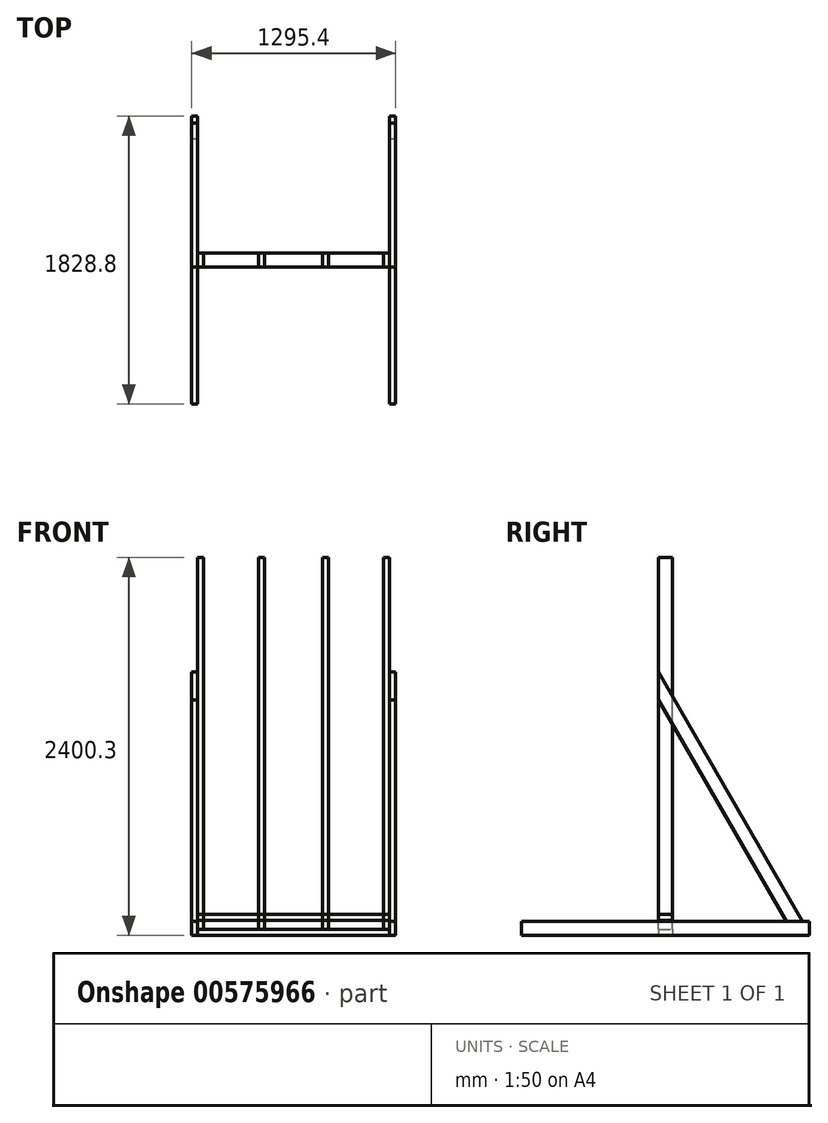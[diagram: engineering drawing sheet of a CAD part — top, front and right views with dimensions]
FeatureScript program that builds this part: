
annotation { "Feature Type Name" : "Feature", "Feature Type Description" : "" }
export const myFeature = defineFeature(function(context is Context, id is Id, definition is map)
    precondition{}
    {
        {
            var Q0;
            Q0=qCreatedBy(makeId("Front.planeOp"),FACE);
            var sketch = newSketch(context, id + "F0", { "sketchPlane" : qUnion([Q0])});
            skLineSegment(sketch, "E0.bottom", {"start": v(0, 0) * mm, "end": v(38.1, 0) * mm});
            skLineSegment(sketch, "E0.top", {"start": v(0, 2362.2) * mm, "end": v(38.1, 2362.2) * mm});
            skLineSegment(sketch, "E0.left", {"start": v(0, 0) * mm, "end": v(0, 2362.2) * mm});
            skLineSegment(sketch, "E0.right", {"start": v(38.1, 0) * mm, "end": v(38.1, 2362.2) * mm});
            skSolve(sketch);
        }
        {
            var Q0;
            Q0 = qSketchRegion(id + "F0", true);
            extrude(context, id + "F1", {"entities" : qUnion([Q0]), "depth" : 88.9 * mm, "offsetDistance" : 25.4 * mm});
        }
        {
            var Q0;
            Q0=makeQuery(id+"F1.opExtrude","SWEPT_BODY",BODY,{"disambiguationData":[OSD([sQuery(id+"F0.wireOp",EDGE,"E0.bottom"),sQuery(id+"F0.wireOp",EDGE,"E0.top"),sQuery(id+"F0.wireOp",EDGE,"E0.left"),sQuery(id+"F0.wireOp",EDGE,"E0.right")])]});
            transform(context, id + "F2", {"entities" : qUnion([Q0]), "transformType" : TransformType.TRANSLATION_3D, "dx" : 387.35 * mm, "dy" : 0 * mm, "dz" : 0 * mm, "makeCopy" : true});
        }
        {
            var Q0;
            Q0=makeQuery(id+"F2.opPattern","COPY",BODY,{"derivedFrom":makeQuery(id+"F1.opExtrude","SWEPT_BODY",BODY,{"disambiguationData":[OSD([sQuery(id+"F0.wireOp",EDGE,"E0.bottom"),sQuery(id+"F0.wireOp",EDGE,"E0.top"),sQuery(id+"F0.wireOp",EDGE,"E0.left"),sQuery(id+"F0.wireOp",EDGE,"E0.right")])]}),"instanceName":"1"});
            transform(context, id + "F3", {"entities" : qUnion([Q0]), "transformType" : TransformType.TRANSLATION_3D, "dx" : 406.4 * mm, "dy" : 0 * mm, "dz" : 0 * mm, "makeCopy" : true});
        }
        {
            var Q0;
            Q0=makeQuery(id+"F3.opPattern","COPY",BODY,{"derivedFrom":makeQuery(id+"F2.opPattern","COPY",BODY,{"derivedFrom":makeQuery(id+"F1.opExtrude","SWEPT_BODY",BODY,{"disambiguationData":[OSD([sQuery(id+"F0.wireOp",EDGE,"E0.bottom"),sQuery(id+"F0.wireOp",EDGE,"E0.top"),sQuery(id+"F0.wireOp",EDGE,"E0.left"),sQuery(id+"F0.wireOp",EDGE,"E0.right")])]}),"instanceName":"1"}),"instanceName":"1"});
            transform(context, id + "F4", {"entities" : qUnion([Q0]), "transformType" : TransformType.TRANSLATION_3D, "dx" : 387.35 * mm, "dy" : 0 * mm, "dz" : 0 * mm, "makeCopy" : true});
        }
        {
            var Q0;
            Q0=qCreatedBy(makeId("Front.planeOp"),FACE);
            var sketch = newSketch(context, id + "F5", { "sketchPlane" : qUnion([Q0])});
            skLineSegment(sketch, "E1.bottom", {"start": v(0, 0) * mm, "end": v(1219.2, 0) * mm});
            skLineSegment(sketch, "E1.top", {"start": v(0, -38.1) * mm, "end": v(1219.2, -38.1) * mm});
            skLineSegment(sketch, "E1.left", {"start": v(0, 0) * mm, "end": v(0, -38.1) * mm});
            skLineSegment(sketch, "E1.right", {"start": v(1219.2, 0) * mm, "end": v(1219.2, -38.1) * mm});
            skSolve(sketch);
        }
        {
            var Q0;
            Q0 = qSketchRegion(id + "F5", true);
            extrude(context, id + "F6", {"entities" : qUnion([Q0]), "depth" : 88.9 * mm, "offsetDistance" : 25.4 * mm});
        }
        {
            var Q0;
            Q0=makeQuery(id+"F6.opExtrude","SWEPT_BODY",BODY,{"disambiguationData":[OSD([sQuery(id+"F5.wireOp",EDGE,"E1.bottom"),sQuery(id+"F5.wireOp",EDGE,"E1.top"),sQuery(id+"F5.wireOp",EDGE,"E1.left"),sQuery(id+"F5.wireOp",EDGE,"E1.right")])]});
            transform(context, id + "F7", {"entities" : qUnion([Q0]), "transformType" : TransformType.TRANSLATION_3D, "dx" : 0 * mm, "dy" : 0 * mm, "dz" : ((8 * 12) - 1.5) * mm, "makeCopy" : true});
        }
        {
            var Q0;
            Q0=makeQuery(id+"F6.opExtrude","SWEPT_FACE",FACE,{"disambiguationData":[OSD([sQuery(id+"F5.wireOp",EDGE,"E1.left")])]});
            var sketch = newSketch(context, id + "F8", { "sketchPlane" : qUnion([Q0])});
            skLineSegment(sketch, "E2.bottom", {"start": v(958.85, 50.8) * mm, "end": v(-869.95, 50.8) * mm});
            skLineSegment(sketch, "E2.top", {"start": v(958.85, -38.1) * mm, "end": v(-869.95, -38.1) * mm});
            skLineSegment(sketch, "E2.left", {"start": v(958.85, 50.8) * mm, "end": v(958.85, -38.1) * mm});
            skLineSegment(sketch, "E2.right", {"start": v(-869.95, 50.8) * mm, "end": v(-869.95, -38.1) * mm});
            skSolve(sketch);
        }
        {
            var Q0;
            Q0 = qSketchRegion(id + "F8", true);
            extrude(context, id + "F9", {"entities" : qUnion([Q0]), "depth" : 38.1 * mm, "offsetDistance" : 25.4 * mm});
        }
        {
            var Q0;
            Q0=makeQuery(id+"F9.opExtrude","SWEPT_BODY",BODY,{"disambiguationData":[OSD([sQuery(id+"F8.wireOp",EDGE,"E2.bottom"),sQuery(id+"F8.wireOp",EDGE,"E2.top"),sQuery(id+"F8.wireOp",EDGE,"E2.left"),sQuery(id+"F8.wireOp",EDGE,"E2.right")])]});
            transform(context, id + "F10", {"entities" : qUnion([Q0]), "transformType" : TransformType.TRANSLATION_3D, "dx" : 1257.3 * mm, "dy" : 0 * mm, "dz" : 0 * mm, "makeCopy" : true});
        }
        {
            var Q0;
            Q0=makeQuery(id+"F10.opPattern","COPY",FACE,{"derivedFrom":makeQuery(id+"F9.opExtrude","CAP_FACE",FACE,{"disambiguationData":[OSD([sQuery(id+"F8.wireOp",EDGE,"E2.bottom"),sQuery(id+"F8.wireOp",EDGE,"E2.top"),sQuery(id+"F8.wireOp",EDGE,"E2.left"),sQuery(id+"F8.wireOp",EDGE,"E2.right")])],"isStart":false}),"instanceName":"1"});
            var sketch = newSketch(context, id + "F11", { "sketchPlane" : qUnion([Q0])});
            skLineSegment(sketch, "E3", {"start": v(-825.5, 50.8) * mm, "end": v(0, 1480.6) * mm});
            skLineSegment(sketch, "E4", {"start": v(0, 1480.6) * mm, "end": v(0, 1302.8) * mm});
            skLineSegment(sketch, "E5", {"start": v(0, 1302.8) * mm, "end": v(-722.85, 50.8) * mm});
            skLineSegment(sketch, "E6", {"start": v(-825.5, 50.8) * mm, "end": v(-722.85, 50.8) * mm});
            skLineSegment(sketch, "E7", {"start": v(0, 1480.6) * mm, "end": v(88.9, 1634.59) * mm});
            skLineSegment(sketch, "E8", {"start": v(0, 1302.8) * mm, "end": v(88.9, 1456.79) * mm});
            skLineSegment(sketch, "E9", {"start": v(88.9, 1634.59) * mm, "end": v(88.9, 1456.79) * mm});
            skSolve(sketch);
        }
        {
            var Q0;
            Q0 = qSketchRegion(id + "F11", true);
            extrude(context, id + "F12", {"entities" : qUnion([Q0]), "oppositeDirection" : true, "depth" : 38.1 * mm, "offsetDistance" : 25.4 * mm});
        }
        {
            var Q0;
            Q0=makeQuery(id+"F12.opExtrude","SWEPT_BODY",BODY,{"disambiguationData":[OSD([sQuery(id+"F11.wireOp",EDGE,"E3"),sQuery(id+"F11.wireOp",EDGE,"E4"),sQuery(id+"F11.wireOp",EDGE,"E5"),sQuery(id+"F11.wireOp",EDGE,"1W0fkmu6-52x2-68E4-ANrA-ky8dyzSj9vcL")])]});
            transform(context, id + "F13", {"entities" : qUnion([Q0]), "transformType" : TransformType.TRANSLATION_3D, "dx" : -1257.3 * mm, "dy" : 0 * mm, "dz" : 0 * mm, "makeCopy" : true});
        }
        {
            var Q0;
            Q0=qCreatedBy(makeId("Right.planeOp"),FACE);
            var sketch = newSketch(context, id + "F14", { "sketchPlane" : qUnion([Q0])});
            skLineSegment(sketch, "E10.bottom", {"start": v(0, 1803.4) * mm, "end": v(-1981.2, 1803.4) * mm});
            skLineSegment(sketch, "E10.top", {"start": v(0, 1892.3) * mm, "end": v(-1981.2, 1892.3) * mm});
            skLineSegment(sketch, "E10.left", {"start": v(0, 1803.4) * mm, "end": v(0, 1892.3) * mm});
            skLineSegment(sketch, "E10.right", {"start": v(-1981.2, 1803.4) * mm, "end": v(-1981.2, 1892.3) * mm});
            skSolve(sketch);
        }
        {
            var Q0;
            Q0 = qSketchRegion(id + "F14", true);
            extrude(context, id + "F15", {"entities" : qUnion([Q0]), "oppositeDirection" : true, "depth" : 38.1 * mm, "offsetDistance" : 25.4 * mm});
        }
        {
            var Q0;
            Q0=makeQuery(id+"F15.opExtrude","SWEPT_BODY",BODY,{"disambiguationData":[OSD([sQuery(id+"F14.wireOp",EDGE,"E10.bottom"),sQuery(id+"F14.wireOp",EDGE,"E10.top"),sQuery(id+"F14.wireOp",EDGE,"E10.left"),sQuery(id+"F14.wireOp",EDGE,"E10.right")])]});
            transform(context, id + "F16", {"entities" : qUnion([Q0]), "transformType" : TransformType.TRANSLATION_3D, "dx" : 1257.3 * mm, "dy" : 0 * mm, "dz" : 0 * mm, "makeCopy" : true});
        }
        {
            var Q0;
            Q0=makeQuery(id+"F15.opExtrude","SWEPT_BODY",BODY,{"disambiguationData":[OSD([sQuery(id+"F14.wireOp",EDGE,"E10.bottom"),sQuery(id+"F14.wireOp",EDGE,"E10.top"),sQuery(id+"F14.wireOp",EDGE,"E10.left"),sQuery(id+"F14.wireOp",EDGE,"E10.right")])]});
            transform(context, id + "F17", {"entities" : qUnion([Q0]), "transformType" : TransformType.TRANSLATION_3D, "dx" : 0 * mm, "dy" : 0 * mm, "dz" : -1524 * mm, "makeCopy" : true});
        }
        {
            var Q0;
            Q0=makeQuery(id+"F17.opPattern","COPY",BODY,{"derivedFrom":makeQuery(id+"F15.opExtrude","SWEPT_BODY",BODY,{"disambiguationData":[OSD([sQuery(id+"F14.wireOp",EDGE,"E10.bottom"),sQuery(id+"F14.wireOp",EDGE,"E10.top"),sQuery(id+"F14.wireOp",EDGE,"E10.left"),sQuery(id+"F14.wireOp",EDGE,"E10.right")])]}),"instanceName":"1"});
            transform(context, id + "F18", {"entities" : qUnion([Q0]), "transformType" : TransformType.TRANSLATION_3D, "dx" : 1257.3 * mm, "dy" : 0 * mm, "dz" : 0 * mm, "makeCopy" : true});
        }
        {
            var Q0;
            Q0=makeQuery(id+"F18.opPattern","COPY",FACE,{"derivedFrom":makeQuery(id+"F17.opPattern","COPY",FACE,{"derivedFrom":makeQuery(id+"F15.opExtrude","CAP_FACE",FACE,{"disambiguationData":[OSD([sQuery(id+"F14.wireOp",EDGE,"E10.bottom"),sQuery(id+"F14.wireOp",EDGE,"E10.top"),sQuery(id+"F14.wireOp",EDGE,"E10.left"),sQuery(id+"F14.wireOp",EDGE,"E10.right")])],"isStart":true}),"instanceName":"1"}),"instanceName":"1"});
            var sketch = newSketch(context, id + "F19", { "sketchPlane" : qUnion([Q0])});
            skLineSegment(sketch, "E11", {"start": v(-1900.94, 1930.52) * mm, "end": v(-1114.62, 279.4) * mm});
            skLineSegment(sketch, "E12", {"start": v(-1114.62, 279.4) * mm, "end": v(-1194.88, 241.18) * mm});
            skLineSegment(sketch, "E13", {"start": v(-1981.2, 1892.3) * mm, "end": v(-1194.88, 241.18) * mm});
            skLineSegment(sketch, "E14", {"start": v(-1900.94, 1930.52) * mm, "end": v(-1981.2, 1892.3) * mm});
            skSolve(sketch);
        }
        {
            var Q0;
            Q0 = qSketchRegion(id + "F19", true);
            extrude(context, id + "F20", {"entities" : qUnion([Q0]), "depth" : 38.1 * mm, "offsetDistance" : 25.4 * mm});
        }
        {
            var Q0;
            Q0=makeQuery(id+"F20.opExtrude","SWEPT_BODY",BODY,{"disambiguationData":[OSD([sQuery(id+"F19.wireOp",EDGE,"E11"),sQuery(id+"F19.wireOp",EDGE,"E12"),sQuery(id+"F19.wireOp",EDGE,"E13"),sQuery(id+"F19.wireOp",EDGE,"E14")])]});
            transform(context, id + "F21", {"entities" : qUnion([Q0]), "transformType" : TransformType.TRANSLATION_3D, "dx" : -1333.5 * mm, "dy" : 0 * mm, "dz" : 0 * mm, "makeCopy" : true});
        }
        {
            var Q0;
            Q0=makeQuery(id+"F21.opPattern","COPY",BODY,{"derivedFrom":makeQuery(id+"F20.opExtrude","SWEPT_BODY",BODY,{"disambiguationData":[OSD([sQuery(id+"F19.wireOp",EDGE,"E11"),sQuery(id+"F19.wireOp",EDGE,"E12"),sQuery(id+"F19.wireOp",EDGE,"E13"),sQuery(id+"F19.wireOp",EDGE,"E14")])]}),"instanceName":"1"});
            deleteBodies(context, id + "F22", {"entities" : qUnion([Q0])});
        }
        {
            var Q0;
            Q0=makeQuery(id+"F20.opExtrude","SWEPT_BODY",BODY,{"disambiguationData":[OSD([sQuery(id+"F19.wireOp",EDGE,"E11"),sQuery(id+"F19.wireOp",EDGE,"E12"),sQuery(id+"F19.wireOp",EDGE,"E13"),sQuery(id+"F19.wireOp",EDGE,"E14")])]});
            deleteBodies(context, id + "F23", {"entities" : qUnion([Q0])});
        }
        {
            var Q0;
            Q0=makeQuery(id+"F18.opPattern","COPY",BODY,{"derivedFrom":makeQuery(id+"F17.opPattern","COPY",BODY,{"derivedFrom":makeQuery(id+"F15.opExtrude","SWEPT_BODY",BODY,{"disambiguationData":[OSD([sQuery(id+"F14.wireOp",EDGE,"E10.bottom"),sQuery(id+"F14.wireOp",EDGE,"E10.top"),sQuery(id+"F14.wireOp",EDGE,"E10.left"),sQuery(id+"F14.wireOp",EDGE,"E10.right")])]}),"instanceName":"1"}),"instanceName":"1"});
            deleteBodies(context, id + "F24", {"entities" : qUnion([Q0])});
        }
        {
            var Q0;
            Q0=makeQuery(id+"F17.opPattern","COPY",BODY,{"derivedFrom":makeQuery(id+"F15.opExtrude","SWEPT_BODY",BODY,{"disambiguationData":[OSD([sQuery(id+"F14.wireOp",EDGE,"E10.bottom"),sQuery(id+"F14.wireOp",EDGE,"E10.top"),sQuery(id+"F14.wireOp",EDGE,"E10.left"),sQuery(id+"F14.wireOp",EDGE,"E10.right")])]}),"instanceName":"1"});
            deleteBodies(context, id + "F25", {"entities" : qUnion([Q0])});
        }
        {
            var Q0;
            Q0=makeQuery(id+"F16.opPattern","COPY",BODY,{"derivedFrom":makeQuery(id+"F15.opExtrude","SWEPT_BODY",BODY,{"disambiguationData":[OSD([sQuery(id+"F14.wireOp",EDGE,"E10.bottom"),sQuery(id+"F14.wireOp",EDGE,"E10.top"),sQuery(id+"F14.wireOp",EDGE,"E10.left"),sQuery(id+"F14.wireOp",EDGE,"E10.right")])]}),"instanceName":"1"});
            deleteBodies(context, id + "F26", {"entities" : qUnion([Q0])});
        }
        {
            var Q0;
            Q0=makeQuery(id+"F15.opExtrude","SWEPT_BODY",BODY,{"disambiguationData":[OSD([sQuery(id+"F14.wireOp",EDGE,"E10.bottom"),sQuery(id+"F14.wireOp",EDGE,"E10.top"),sQuery(id+"F14.wireOp",EDGE,"E10.left"),sQuery(id+"F14.wireOp",EDGE,"E10.right")])]});
            deleteBodies(context, id + "F27", {"entities" : qUnion([Q0])});
        }
    });
